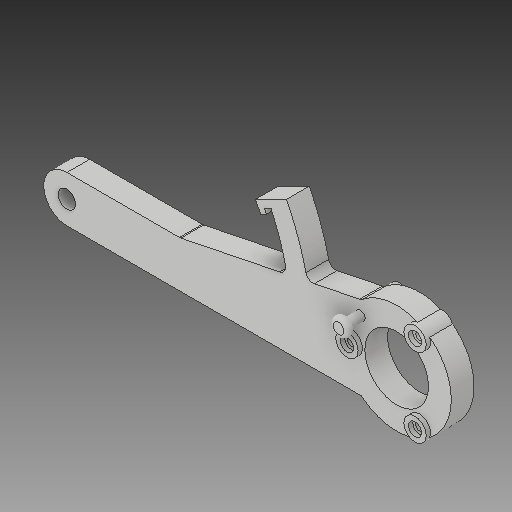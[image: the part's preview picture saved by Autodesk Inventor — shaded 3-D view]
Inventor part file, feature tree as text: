
AUTODESK INVENTOR PART (.ipt)
format: ipt  version: 2019 (Build 230136000, 136)  size: 214,528 bytes
history: native  units: in
note: dims shown in document units (in); Inventor stores cm internally (conversion verified against a paired STEP export)
features: sketch x9, other x3
ambient origin geometry x8: Origin, YZ Plane, XZ Plane, XY Plane, X Axis, Y Axis, Z Axis, Center Point
bodies: Solid1 (feature_tree)
feature tree (12):
  other  "Shock_Arm.ipt"
  other  "Solid1::Shock_Arm.ipt"
  other  "TaggingFeature1"
  sketch  "Sketch1"  dims[d0=0.3937in]
  sketch  "Sketch2"
  sketch  "Sketch3"
  sketch  "Sketch5"
  sketch  "Sketch4"
  sketch  "Sketch6"
  sketch  "Sketch7"
  sketch  "Sketch8"
  sketch  "Sketch10"
